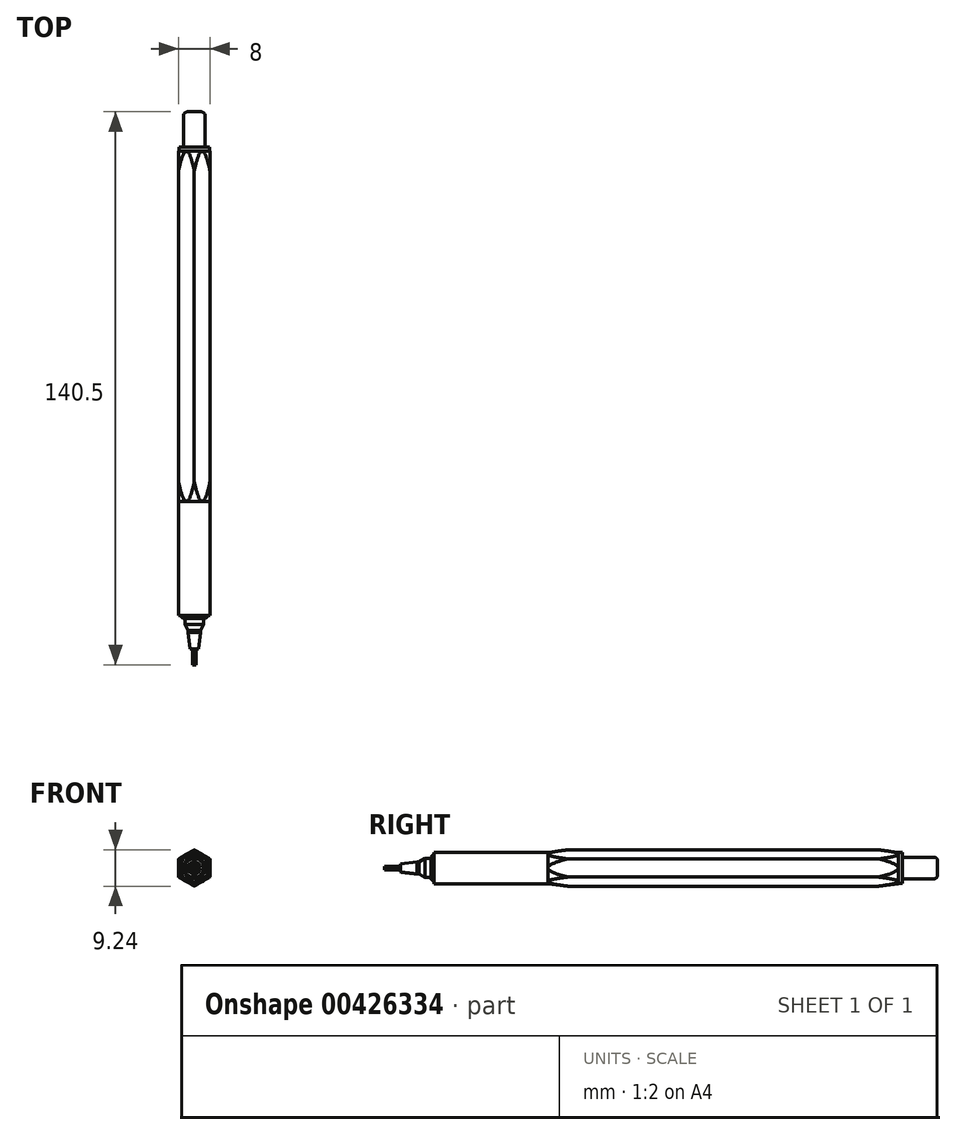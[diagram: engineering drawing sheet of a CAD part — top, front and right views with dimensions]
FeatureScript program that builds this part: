
annotation { "Feature Type Name" : "Feature", "Feature Type Description" : "" }
export const myFeature = defineFeature(function(context is Context, id is Id, definition is map)
    precondition{}
    {
        {
            var Q0;
            Q0=qCreatedBy(makeId("Front.planeOp"),FACE);
            var sketch = newSketch(context, id + "F0", { "sketchPlane" : qUnion([Q0])});
            skCircle(sketch, "E0.cCircle", {"center": v(0, 0) * mm, "radius": 4 * mm, "construction": true});
            skLineSegment(sketch, "E0.0", {"start": v(4, 2.3) * mm, "end": v(4, -2.3) * mm});
            skLineSegment(sketch, "E0.1", {"start": v(4, -2.3) * mm, "end": v(0, -4.62) * mm});
            skLineSegment(sketch, "E0.2", {"start": v(0, -4.62) * mm, "end": v(-4, -2.3) * mm});
            skLineSegment(sketch, "E0.3", {"start": v(-4, -2.3) * mm, "end": v(-4, 2.3) * mm});
            skLineSegment(sketch, "E0.4", {"start": v(-4, 2.3) * mm, "end": v(0, 4.62) * mm});
            skLineSegment(sketch, "E0.5", {"start": v(0, 4.62) * mm, "end": v(4, 2.3) * mm});
            skPoint(sketch, "E0.0.midPoint", {"position": v(4, 0) * mm});
            skSolve(sketch);
        }
        {
            var Q0;
            Q0 = qSketchRegion(id + "F0", true);
            extrude(context, id + "F1", {"entities" : qUnion([Q0]), "depth" : 89 * mm});
        }
        {
            var Q0;
            Q0=makeQuery(id+"F1.opExtrude","CAP_FACE",FACE,{"disambiguationData":[OSD([sQuery(id+"F0.wireOp",EDGE,"E0.0"),sQuery(id+"F0.wireOp",EDGE,"E0.1"),sQuery(id+"F0.wireOp",EDGE,"E0.2"),sQuery(id+"F0.wireOp",EDGE,"E0.3"),sQuery(id+"F0.wireOp",EDGE,"E0.4"),sQuery(id+"F0.wireOp",EDGE,"E0.5")])],"isStart":false});
            var sketch = newSketch(context, id + "F2", { "sketchPlane" : qUnion([Q0])});
            skCircle(sketch, "E1", {"center": v(0, 0) * mm, "radius": 4 * mm});
            skSolve(sketch);
        }
        {
            var Q0;
            Q0 = qSketchRegion(id + "F2", true);
            extrude(context, id + "F3", {"entities" : qUnion([Q0]), "operationType" : NewBodyOperationType.ADD, "depth" : 29 * mm});
        }
        {
            var Q0;
            {var subQ0=sQuery(id+"F0.wireOp",EDGE,"E0.5");var subQ1=sQuery(id+"F0.wireOp",EDGE,"E0.4");var subQ2=makeQuery(id+"F1.opExtrude","CAP_FACE",FACE,{"disambiguationData":[OSD([sQuery(id+"F0.wireOp",EDGE,"E0.0"),sQuery(id+"F0.wireOp",EDGE,"E0.1"),sQuery(id+"F0.wireOp",EDGE,"E0.2"),sQuery(id+"F0.wireOp",EDGE,"E0.3"),subQ1,subQ0])],"isStart":false});Q0=makeQuery(id+"F3.boolean.opBoolean","SPLIT",FACE,{"disambiguationData":[TD([subQ2,makeQuery(id+"F1.opExtrude","SWEPT_FACE",FACE,{"disambiguationData":[OSD([subQ1])]}),makeQuery(id+"F1.opExtrude","SWEPT_FACE",FACE,{"disambiguationData":[OSD([subQ0])]}),makeQuery(id+"F3.opExtrude","SWEPT_FACE",FACE,{"disambiguationData":[OSD([sQuery(id+"F2.wireOp",EDGE,"E1")])]})])],"derivedFrom":subQ2});}
            var sketch = newSketch(context, id + "F4", { "sketchPlane" : qUnion([Q0])});
            skCircle(sketch, "E2", {"center": v(0, 0) * mm, "radius": 4 * mm});
            skCircle(sketch, "E3", {"center": v(0, 0) * mm, "radius": 6 * mm});
            skSolve(sketch);
        }
        {
            var Q0;
            Q0 = qSketchRegion(id + "F4", true);
            extrude(context, id + "F5", {"entities" : qUnion([Q0]), "operationType" : NewBodyOperationType.REMOVE, "oppositeDirection" : true, "depth" : 5.2 * mm, "hasDraft" : true, "draftAngle" : 7 * degree, "draftPullDirection" : true});
        }
        {
            var Q0;
            Q0=makeQuery(id+"F1.opExtrude","CAP_FACE",FACE,{"disambiguationData":[OSD([sQuery(id+"F0.wireOp",EDGE,"E0.0"),sQuery(id+"F0.wireOp",EDGE,"E0.1"),sQuery(id+"F0.wireOp",EDGE,"E0.2"),sQuery(id+"F0.wireOp",EDGE,"E0.3"),sQuery(id+"F0.wireOp",EDGE,"E0.4"),sQuery(id+"F0.wireOp",EDGE,"E0.5")])],"isStart":true});
            var sketch = newSketch(context, id + "F6", { "sketchPlane" : qUnion([Q0])});
            skCircle(sketch, "E4", {"center": v(0, 0) * mm, "radius": 4 * mm});
            skCircle(sketch, "E5", {"center": v(0, 0) * mm, "radius": 6 * mm});
            skSolve(sketch);
        }
        {
            var Q0;
            Q0 = qSketchRegion(id + "F6", true);
            extrude(context, id + "F7", {"entities" : qUnion([Q0]), "operationType" : NewBodyOperationType.REMOVE, "oppositeDirection" : true, "depth" : 5.2 * mm, "hasDraft" : true, "draftAngle" : 7 * degree, "draftPullDirection" : true});
        }
        {
            var Q0;
            Q0=makeQuery(id+"F3.opExtrude","CAP_FACE",FACE,{"disambiguationData":[OSD([sQuery(id+"F2.wireOp",EDGE,"E1")])],"isStart":false});
            var sketch = newSketch(context, id + "F8", { "sketchPlane" : qUnion([Q0])});
            skCircle(sketch, "E6", {"center": v(0, 0) * mm, "radius": 3.6 * mm});
            skSolve(sketch);
        }
        {
            var Q0;
            Q0 = qSketchRegion(id + "F8", true);
            extrude(context, id + "F9", {"entities" : qUnion([Q0]), "depth" : .75 * mm, "hasDraft" : true, "draftAngle" : 45 * degree, "draftPullDirection" : true});
        }
        {
            var Q0;
            Q0=makeQuery(id+"F9.opExtrude","CAP_FACE",FACE,{"disambiguationData":[OSD([sQuery(id+"F8.wireOp",EDGE,"E6")])],"isStart":false});
            var sketch = newSketch(context, id + "F10", { "sketchPlane" : qUnion([Q0])});
            skCircle(sketch, "E7", {"center": v(0, 0) * mm, "radius": 2.4 * mm});
            skSolve(sketch);
        }
        {
            var Q0;
            Q0 = qSketchRegion(id + "F10", true);
            extrude(context, id + "F11", {"entities" : qUnion([Q0]), "operationType" : NewBodyOperationType.ADD, "depth" : 1.5 * mm});
        }
        {
            var Q0;
            Q0=makeQuery(id+"F11.opExtrude","CAP_FACE",FACE,{"disambiguationData":[OSD([sQuery(id+"F10.wireOp",EDGE,"E7")])],"isStart":false});
            var sketch = newSketch(context, id + "F12", { "sketchPlane" : qUnion([Q0])});
            skCircle(sketch, "E8", {"center": v(0, 0) * mm, "radius": 2.4 * mm});
            skSolve(sketch);
        }
        {
            var Q0;
            Q0 = qSketchRegion(id + "F12", true);
            extrude(context, id + "F13", {"entities" : qUnion([Q0]), "operationType" : NewBodyOperationType.ADD, "depth" : 1.5 * mm, "hasDraft" : true, "draftAngle" : 30 * degree, "draftPullDirection" : true});
        }
        {
            var Q0;
            Q0=makeQuery(id+"F13.opExtrude","CAP_FACE",FACE,{"disambiguationData":[OSD([sQuery(id+"F12.wireOp",EDGE,"E8")])],"isStart":false});
            var sketch = newSketch(context, id + "F14", { "sketchPlane" : qUnion([Q0])});
            skCircle(sketch, "E9", {"center": v(0, 0) * mm, "radius": 1.53 * mm});
            skSolve(sketch);
        }
        {
            var Q0;
            Q0 = qSketchRegion(id + "F14", true);
            extrude(context, id + "F15", {"entities" : qUnion([Q0]), "operationType" : NewBodyOperationType.ADD, "depth" : .5 * mm});
        }
        {
            var Q0;
            Q0=makeQuery(id+"F15.opExtrude","CAP_FACE",FACE,{"disambiguationData":[OSD([sQuery(id+"F14.wireOp",EDGE,"E9")])],"isStart":false});
            var sketch = newSketch(context, id + "F16", { "sketchPlane" : qUnion([Q0])});
            skCircle(sketch, "E10", {"center": v(0, 0) * mm, "radius": 1.53 * mm});
            skSolve(sketch);
        }
        {
            var Q0;
            Q0 = qSketchRegion(id + "F16", true);
            extrude(context, id + "F17", {"entities" : qUnion([Q0]), "operationType" : NewBodyOperationType.ADD, "depth" : 4.25 * mm, "hasDraft" : true, "draftAngle" : 6.5 * degree, "draftPullDirection" : true});
        }
        {
            var Q0;
            Q0=makeQuery(id+"F17.opExtrude","CAP_FACE",FACE,{"disambiguationData":[OSD([sQuery(id+"F16.wireOp",EDGE,"E10")])],"isStart":false});
            var sketch = newSketch(context, id + "F18", { "sketchPlane" : qUnion([Q0])});
            skCircle(sketch, "E11", {"center": v(0, 0) * mm, "radius": 0.47 * mm});
            skSolve(sketch);
        }
        {
            var Q0;
            Q0 = qSketchRegion(id + "F18", true);
            extrude(context, id + "F19", {"entities" : qUnion([Q0]), "operationType" : NewBodyOperationType.ADD, "depth" : 4 * mm});
        }
        {
            var Q0;
            Q0=makeQuery(id+"F1.opExtrude","CAP_FACE",FACE,{"disambiguationData":[OSD([sQuery(id+"F0.wireOp",EDGE,"E0.0"),sQuery(id+"F0.wireOp",EDGE,"E0.1"),sQuery(id+"F0.wireOp",EDGE,"E0.2"),sQuery(id+"F0.wireOp",EDGE,"E0.3"),sQuery(id+"F0.wireOp",EDGE,"E0.4"),sQuery(id+"F0.wireOp",EDGE,"E0.5")])],"isStart":true});
            var sketch = newSketch(context, id + "F20", { "sketchPlane" : qUnion([Q0])});
            skCircle(sketch, "E12", {"center": v(0, 0) * mm, "radius": 3.9 * mm});
            skSolve(sketch);
        }
        {
            var Q0;
            Q0 = qSketchRegion(id + "F20", true);
            extrude(context, id + "F21", {"entities" : qUnion([Q0]), "depth" : 1 * mm});
        }
        {
            var Q0;
            Q0=makeQuery(id+"F21.opExtrude","CAP_FACE",FACE,{"disambiguationData":[OSD([sQuery(id+"F20.wireOp",EDGE,"E12")])],"isStart":false});
            var sketch = newSketch(context, id + "F22", { "sketchPlane" : qUnion([Q0])});
            skCircle(sketch, "E13", {"center": v(0, 0) * mm, "radius": 2.75 * mm});
            skSolve(sketch);
        }
        {
            var Q0;
            Q0 = qSketchRegion(id + "F22", true);
            extrude(context, id + "F23", {"entities" : qUnion([Q0]), "operationType" : NewBodyOperationType.ADD, "depth" : 9 * mm});
        }
        {
            var Q0;
            Q0=makeQuery(id+"F23.opExtrude","CAP_EDGE",EDGE,{"disambiguationData":[OSD([sQuery(id+"F22.wireOp",EDGE,"E13")])],"isStart":false});
            fillet(context, id + "F24", {"entities" : qUnion([Q0]), "radius" : 1 * mm, "tangentPropagation" : true, "allowEdgeOverflow" : false});
        }
    });
